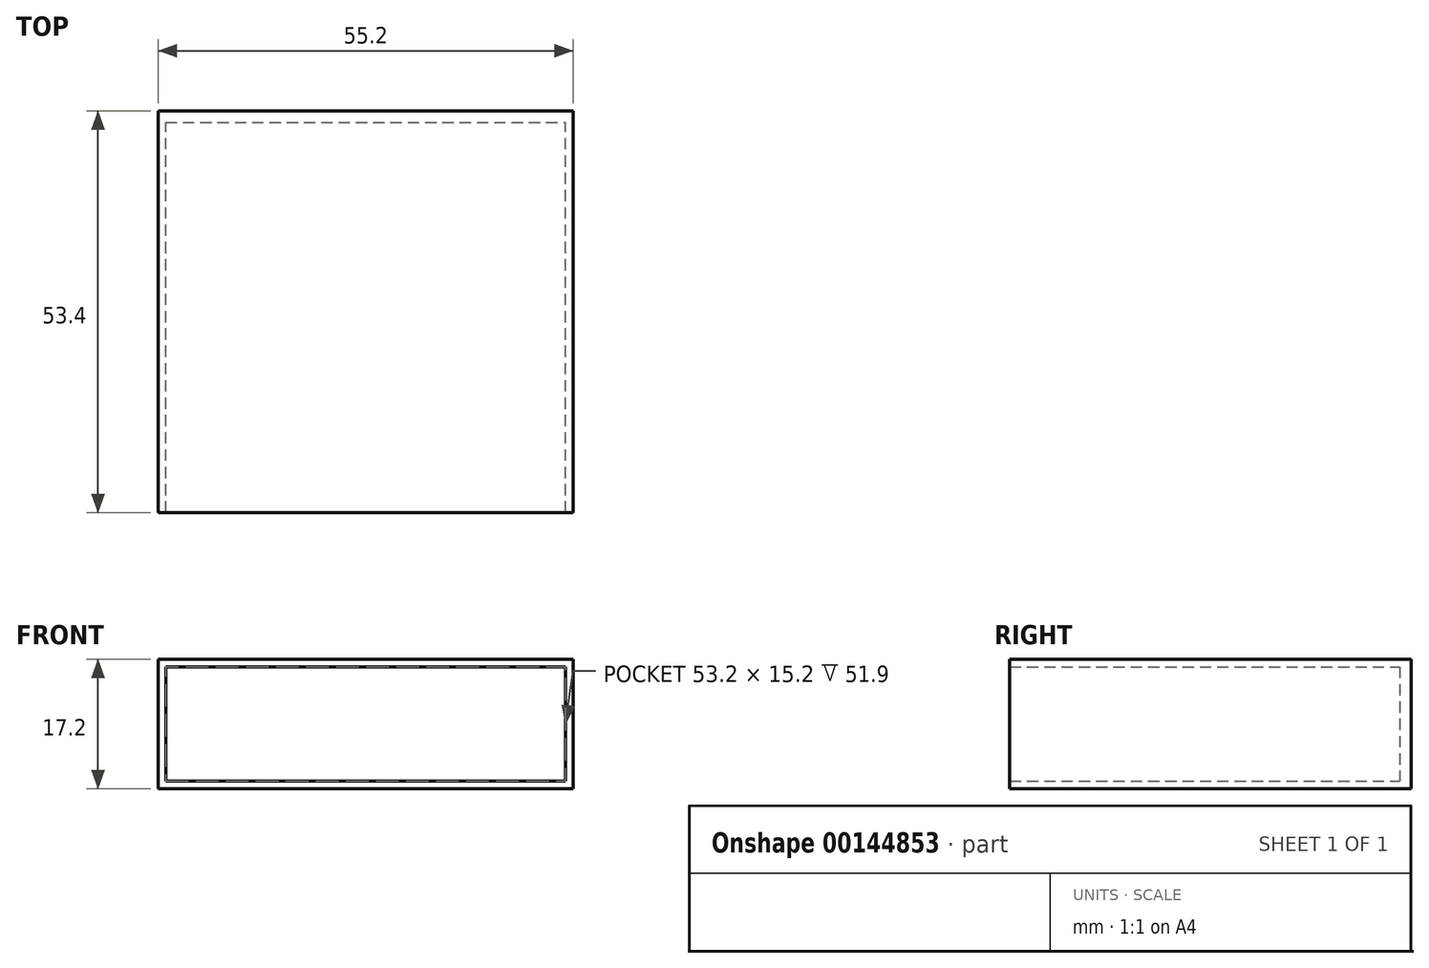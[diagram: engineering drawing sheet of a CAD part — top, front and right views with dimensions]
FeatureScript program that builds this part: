
annotation { "Feature Type Name" : "Feature", "Feature Type Description" : "" }
export const myFeature = defineFeature(function(context is Context, id is Id, definition is map)
    precondition{}
    {
        {
            var Q0;
            Q0=qCreatedBy(makeId("Front.planeOp"),FACE);
            var sketch = newSketch(context, id + "F0", { "sketchPlane" : qUnion([Q0])});
            skLineSegment(sketch, "E0.bottom", {"start": v(-20, 8.79) * mm, "end": v(33.2, 8.79) * mm});
            skLineSegment(sketch, "E0.top", {"start": v(-20, -6.41) * mm, "end": v(33.2, -6.41) * mm});
            skLineSegment(sketch, "E0.left", {"start": v(-20, 8.79) * mm, "end": v(-20, -6.41) * mm});
            skLineSegment(sketch, "E0.right", {"start": v(33.2, 8.79) * mm, "end": v(33.2, -6.41) * mm});
            skLineSegment(sketch, "E1.0", {"start": v(-21, 9.79) * mm, "end": v(34.2, 9.79) * mm});
            skLineSegment(sketch, "E1.1", {"start": v(-21, 9.79) * mm, "end": v(-21, -7.41) * mm});
            skLineSegment(sketch, "E1.2", {"start": v(-21, -7.41) * mm, "end": v(34.2, -7.41) * mm});
            skLineSegment(sketch, "E1.3", {"start": v(34.2, 9.79) * mm, "end": v(34.2, -7.41) * mm});
            skSolve(sketch);
        }
        {
            var Q0;
            Q0 = qSketchRegion(id + "F0", true);
            extrude(context, id + "F1", {"entities" : qUnion([Q0]), "depth" : 53.4 * mm});
        }
        {
            var Q0;
            Q0=makeQuery(id+"F0.imprint","IMPRINT",FACE,{"disambiguationData":[TD([[makeQuery(id+"F0.imprint","IMPRINT",EDGE,{"derivedFrom":sQuery(id+"F0.wireOp",EDGE,"E0.bottom")}),-1.0]])]});
            extrude(context, id + "F2", {"entities" : qUnion([Q0]), "operationType" : NewBodyOperationType.ADD, "depth" : 1.5 * mm});
        }
    });
